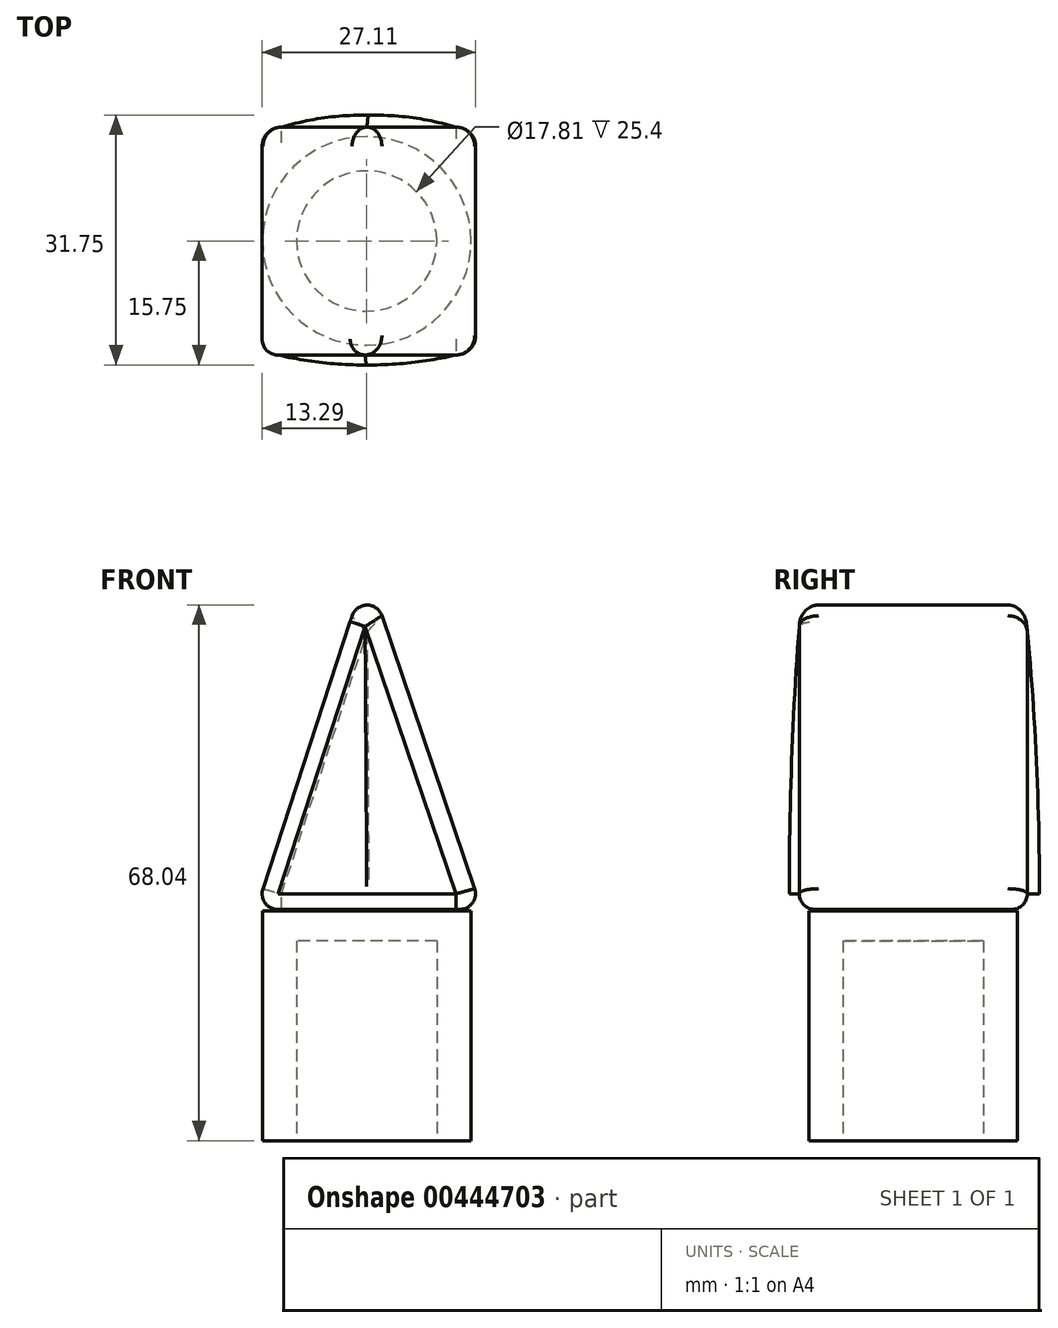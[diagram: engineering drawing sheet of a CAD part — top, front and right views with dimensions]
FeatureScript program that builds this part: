
annotation { "Feature Type Name" : "Feature", "Feature Type Description" : "" }
export const myFeature = defineFeature(function(context is Context, id is Id, definition is map)
    precondition{}
    {
        {
            var Q0;
            Q0=qCreatedBy(makeId("Top.planeOp"),FACE);
            var sketch = newSketch(context, id + "F0", { "sketchPlane" : qUnion([Q0])});
            skCircle(sketch, "E0", {"center": v(0, 0) * mm, "radius": 13.24 * mm});
            skSolve(sketch);
        }
        {
            var Q0;
            Q0 = qSketchRegion(id + "F0", true);
            extrude(context, id + "F1", {"entities" : qUnion([Q0]), "depth" : 29.2 * mm});
        }
        {
            var Q0;
            Q0=qCreatedBy(makeId("Front.planeOp"),FACE);
            var sketch = newSketch(context, id + "F2", { "sketchPlane" : qUnion([Q0])});
            skLineSegment(sketch, "E1", {"start": v(-14.04, 29.37) * mm, "end": v(0, 72.36) * mm});
            skLineSegment(sketch, "E2", {"start": v(0, 72.36) * mm, "end": v(14.61, 29.37) * mm});
            skLineSegment(sketch, "E3", {"start": v(-14.04, 29.37) * mm, "end": v(14.61, 29.37) * mm});
            skSolve(sketch);
        }
        {
            var Q0;
            Q0 = qSketchRegion(id + "F2", true);
            extrude(context, id + "F3", {"entities" : qUnion([Q0]), "depth" : 14.48 * mm, "hasSecondDirection" : true, "secondDirectionOppositeDirection" : true, "secondDirectionDepth" : 14.48 * mm});
        }
        {
            var Q0;
            Q0=makeQuery(id+"F3.opExtrude","SWEPT_EDGE",EDGE,{"disambiguationData":[OSD([sQuery(id+"F2.wireOp",EDGE,"E1"),sQuery(id+"F2.wireOp",EDGE,"E2")])]});
            var Q1;
            Q1=makeQuery(id+"F3.opExtrude","SWEPT_EDGE",EDGE,{"disambiguationData":[OSD([sQuery(id+"F2.wireOp",EDGE,"E2"),sQuery(id+"F2.wireOp",EDGE,"E3")])]});
            var Q2;
            Q2=makeQuery(id+"F3.opExtrude","SWEPT_EDGE",EDGE,{"disambiguationData":[OSD([sQuery(id+"F2.wireOp",EDGE,"E1"),sQuery(id+"F2.wireOp",EDGE,"E3")])]});
            var Q3;
            Q3=makeQuery(id+"F3.opExtrude","CAP_EDGE",EDGE,{"disambiguationData":[OSD([sQuery(id+"F2.wireOp",EDGE,"E3")])],"isStart":true});
            var Q4;
            Q4=makeQuery(id+"F3.opExtrude","CAP_EDGE",EDGE,{"disambiguationData":[OSD([sQuery(id+"F2.wireOp",EDGE,"E3")])],"isStart":false});
            var Q5;
            Q5=makeQuery(id+"F3.opExtrude","CAP_EDGE",EDGE,{"disambiguationData":[OSD([sQuery(id+"F2.wireOp",EDGE,"E1")])],"isStart":false});
            fillet(context, id + "F4", {"entities" : qUnion([Q0, Q1, Q2, Q3, Q4, Q5]), "radius" : 2 * mm, "tangentPropagation" : true, "allowEdgeOverflow" : false});
        }
        {
            var Q0;
            Q0=qCreatedBy(makeId("Top.planeOp"),FACE);
            var sketch = newSketch(context, id + "F5", { "sketchPlane" : qUnion([Q0])});
            skCircle(sketch, "E4", {"center": v(0, 0) * mm, "radius": 8.9 * mm});
            skSolve(sketch);
        }
        {
            var Q0;
            Q0 = qSketchRegion(id + "F5", true);
            extrude(context, id + "F6", {"entities" : qUnion([Q0]), "operationType" : NewBodyOperationType.REMOVE, "depth" : 25.4 * mm});
        }
        {
            var Q0;
            Q0=makeQuery(id+"F3.opExtrude","CAP_EDGE",EDGE,{"disambiguationData":[OSD([sQuery(id+"F2.wireOp",EDGE,"E2")])],"isStart":false});
            var Q1;
            Q1=makeQuery(id+"F3.opExtrude","CAP_EDGE",EDGE,{"disambiguationData":[OSD([sQuery(id+"F2.wireOp",EDGE,"E2")])],"isStart":true});
            fillet(context, id + "F7", {"entities" : qUnion([Q0, Q1]), "radius" : 2.45 * mm, "tangentPropagation" : true, "allowEdgeOverflow" : false});
        }
        {
            var Q0;
            Q0=makeQuery(id+"F3.opExtrude","CAP_FACE",FACE,{"disambiguationData":[OSD([sQuery(id+"F2.wireOp",EDGE,"E1"),sQuery(id+"F2.wireOp",EDGE,"E2"),sQuery(id+"F2.wireOp",EDGE,"E3")])],"isStart":true});
            extrude(context, id + "F8", {"entities" : qUnion([Q0]), "operationType" : NewBodyOperationType.ADD, "depth" : 1.52 * mm});
        }
        {
            var Q0;
            {var subQ0=sQuery(id+"F2.wireOp",EDGE,"E3");var subQ1=sQuery(id+"F2.wireOp",EDGE,"E2");var subQ2=sQuery(id+"F2.wireOp",EDGE,"E1");Q0=makeQuery(id+"F8.opExtrude","CAP_EDGE",EDGE,{"disambiguationData":[OSD([subQ2,subQ1,subQ0]),TDD([makeQuery(id+"F7.opFillet","BLEND_EDGE",EDGE,{"blendedFrom":[makeQuery(id+"F3.opExtrude","CAP_EDGE",EDGE,{"disambiguationData":[OSD([subQ2])],"isStart":true}),makeQuery(id+"F3.opExtrude","CAP_FACE",FACE,{"disambiguationData":[OSD([subQ2,subQ1,subQ0])],"isStart":true})],"blendedInto":[makeQuery(id+"F3.opExtrude","CAP_FACE",FACE,{"disambiguationData":[OSD([subQ2,subQ1,subQ0])],"isStart":true})]})])],"isStart":false});}
            var Q1;
            {var subQ0=sQuery(id+"F2.wireOp",EDGE,"E3");var subQ1=sQuery(id+"F2.wireOp",EDGE,"E2");var subQ2=sQuery(id+"F2.wireOp",EDGE,"E1");Q1=makeQuery(id+"F8.opExtrude","CAP_EDGE",EDGE,{"disambiguationData":[OSD([subQ2,subQ1,subQ0]),TDD([makeQuery(id+"F7.opFillet","BLEND_EDGE",EDGE,{"blendedFrom":[makeQuery(id+"F3.opExtrude","CAP_EDGE",EDGE,{"disambiguationData":[OSD([subQ1])],"isStart":true}),makeQuery(id+"F3.opExtrude","CAP_FACE",FACE,{"disambiguationData":[OSD([subQ2,subQ1,subQ0])],"isStart":true})],"blendedInto":[makeQuery(id+"F3.opExtrude","CAP_FACE",FACE,{"disambiguationData":[OSD([subQ2,subQ1,subQ0])],"isStart":true})]})])],"isStart":false});}
            fillet(context, id + "F9", {"entities" : qUnion([Q0, Q1]), "radius" : 33.73 * mm, "tangentPropagation" : true, "allowEdgeOverflow" : false});
        }
        {
            var Q0;
            Q0=makeQuery(id+"F3.opExtrude","CAP_FACE",FACE,{"disambiguationData":[OSD([sQuery(id+"F2.wireOp",EDGE,"E1"),sQuery(id+"F2.wireOp",EDGE,"E2"),sQuery(id+"F2.wireOp",EDGE,"E3")])],"isStart":false});
            extrude(context, id + "F10", {"entities" : qUnion([Q0]), "operationType" : NewBodyOperationType.ADD, "depth" : 1.27 * mm});
        }
        {
            var Q0;
            {var subQ0=sQuery(id+"F2.wireOp",EDGE,"E3");var subQ1=sQuery(id+"F2.wireOp",EDGE,"E2");var subQ2=sQuery(id+"F2.wireOp",EDGE,"E1");Q0=makeQuery(id+"F10.opExtrude","CAP_EDGE",EDGE,{"disambiguationData":[OSD([subQ2,subQ1,subQ0]),TDD([makeQuery(id+"F4.opFillet","BLEND_EDGE",EDGE,{"blendedFrom":[makeQuery(id+"F3.opExtrude","CAP_EDGE",EDGE,{"disambiguationData":[OSD([subQ2])],"isStart":false}),makeQuery(id+"F3.opExtrude","CAP_FACE",FACE,{"disambiguationData":[OSD([subQ2,subQ1,subQ0])],"isStart":false})],"blendedInto":[makeQuery(id+"F3.opExtrude","CAP_FACE",FACE,{"disambiguationData":[OSD([subQ2,subQ1,subQ0])],"isStart":false})]})])],"isStart":false});}
            var Q1;
            {var subQ0=sQuery(id+"F2.wireOp",EDGE,"E3");var subQ1=sQuery(id+"F2.wireOp",EDGE,"E2");var subQ2=sQuery(id+"F2.wireOp",EDGE,"E1");Q1=makeQuery(id+"F10.opExtrude","CAP_EDGE",EDGE,{"disambiguationData":[OSD([subQ2,subQ1,subQ0]),TDD([makeQuery(id+"F7.opFillet","BLEND_EDGE",EDGE,{"blendedFrom":[makeQuery(id+"F3.opExtrude","CAP_EDGE",EDGE,{"disambiguationData":[OSD([subQ1])],"isStart":false}),makeQuery(id+"F3.opExtrude","CAP_FACE",FACE,{"disambiguationData":[OSD([subQ2,subQ1,subQ0])],"isStart":false})],"blendedInto":[makeQuery(id+"F3.opExtrude","CAP_FACE",FACE,{"disambiguationData":[OSD([subQ2,subQ1,subQ0])],"isStart":false})]})])],"isStart":false});}
            fillet(context, id + "F11", {"entities" : qUnion([Q0, Q1]), "radius" : 43.54 * mm, "tangentPropagation" : true, "allowEdgeOverflow" : false});
        }
    });
